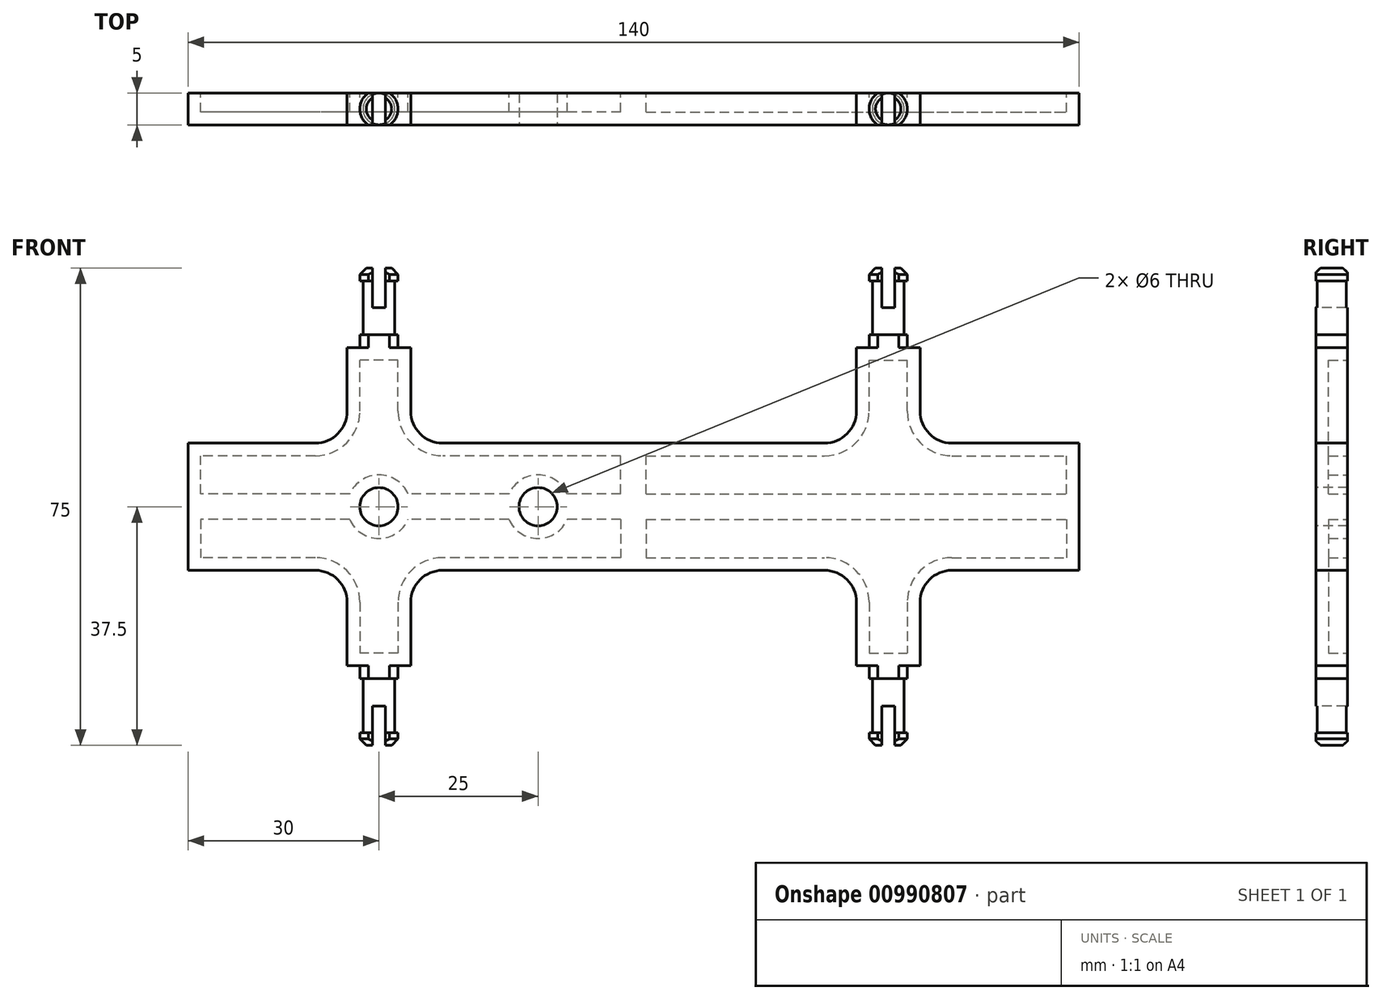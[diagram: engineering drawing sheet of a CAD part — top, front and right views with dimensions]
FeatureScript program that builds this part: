
annotation { "Feature Type Name" : "Feature", "Feature Type Description" : "" }
export const myFeature = defineFeature(function(context is Context, id is Id, definition is map)
    precondition{}
    {
        {
            var Q0;
            Q0=qCreatedBy(makeId("Front.planeOp"),FACE);
            var sketch = newSketch(context, id + "F0", { "sketchPlane" : qUnion([Q0])});
            skLineSegment(sketch, "E0.bottom", {"start": v(0, 0) * mm, "end": v(70, 0) * mm});
            skLineSegment(sketch, "E0.top", {"start": v(0, 10) * mm, "end": v(30, 10) * mm});
            skLineSegment(sketch, "E0.left", {"start": v(0, 0) * mm, "end": v(0, 10) * mm});
            skLineSegment(sketch, "E0.right", {"start": v(70, 0) * mm, "end": v(70, 10) * mm});
            skLineSegment(sketch, "E1.top", {"start": v(35, 25) * mm, "end": v(45, 25) * mm});
            skLineSegment(sketch, "E1.left", {"start": v(35, 15) * mm, "end": v(35, 25) * mm});
            skLineSegment(sketch, "E1.right", {"start": v(45, 15) * mm, "end": v(45, 25) * mm});
            skLineSegment(sketch, "E2.trimOffspring", {"start": v(50, 10) * mm, "end": v(70, 10) * mm});
            skPoint(sketch, "E3.visualSharp", {"position": v(35, 10) * mm});
            skArc(sketch, "E3.filletArc", {"start": v(30, 10) * mm, "mid": v(33.54, 11.46) * mm, "end": v(35, 15) * mm});
            skPoint(sketch, "E4.visualSharp", {"position": v(45, 10) * mm});
            skArc(sketch, "E4.filletArc", {"start": v(45, 15) * mm, "mid": v(46.46, 11.46) * mm, "end": v(50, 10) * mm});
            skSolve(sketch);
        }
        {
            var Q0;
            Q0 = qSketchRegion(id + "F0", true);
            extrude(context, id + "F1", {"entities" : qUnion([Q0]), "endBound" : BoundingType.SYMMETRIC, "depth" : 5 * mm, "offsetDistance" : 25 * mm});
        }
        {
            var Q0;
            Q0=makeQuery(id+"F1.opExtrude","CAP_FACE",FACE,{"disambiguationData":[OSD([sQuery(id+"F0.wireOp",EDGE,"E0.bottom"),sQuery(id+"F0.wireOp",EDGE,"E0.top"),sQuery(id+"F0.wireOp",EDGE,"E0.left"),sQuery(id+"F0.wireOp",EDGE,"E0.right"),sQuery(id+"F0.wireOp",EDGE,"E1.top"),sQuery(id+"F0.wireOp",EDGE,"E1.left"),sQuery(id+"F0.wireOp",EDGE,"E1.right"),sQuery(id+"F0.wireOp",EDGE,"E2.trimOffspring"),sQuery(id+"F0.wireOp",EDGE,"E3.filletArc"),sQuery(id+"F0.wireOp",EDGE,"E4.filletArc")])],"isStart":true});
            shell(context, id + "F2", {"entities" : qUnion([Q0]), "thickness" : 2 * mm});
        }
        {
            var Q0;
            Q0=qCreatedBy(makeId("Front.planeOp"),FACE);
            var sketch = newSketch(context, id + "F3", { "sketchPlane" : qUnion([Q0])});
            skLineSegment(sketch, "E5", {"start": v(40, 25) * mm, "end": v(40, 37.5) * mm});
            skLineSegment(sketch, "E6", {"start": v(40, 37.5) * mm, "end": v(43, 37.5) * mm});
            skLineSegment(sketch, "E7", {"start": v(43, 37.5) * mm, "end": v(43, 35.5) * mm});
            skLineSegment(sketch, "E8", {"start": v(43, 35.5) * mm, "end": v(42.5, 35.5) * mm});
            skLineSegment(sketch, "E9", {"start": v(42.5, 35.5) * mm, "end": v(42.5, 27) * mm});
            skLineSegment(sketch, "E10", {"start": v(42.5, 27) * mm, "end": v(43, 27) * mm});
            skLineSegment(sketch, "E11", {"start": v(43, 27) * mm, "end": v(43, 25) * mm});
            skLineSegment(sketch, "E12", {"start": v(43, 25) * mm, "end": v(40, 25) * mm});
            skSolve(sketch);
        }
        {
            var Q0;
            Q0=makeQuery(id+"F3.imprint","IMPRINT",FACE,{"disambiguationData":[TD([[makeQuery(id+"F3.imprint","IMPRINT",EDGE,{"derivedFrom":sQuery(id+"F3.wireOp",EDGE,"E5")}),-1.0]])]});
            var Q1;
            Q1=sQuery(id+"F3.wireOp",EDGE,"E5");
            revolve(context, id + "F4", {"operationType" : NewBodyOperationType.ADD, "surfaceOperationType" : NewSurfaceOperationType.NEW, "entities" : qUnion([Q0]), "axis" : qUnion([Q1]), "revolveType" : RevolveType.FULL});
        }
        {
            var Q0;
            Q0=makeQuery(id+"F4.opRevolve","SWEPT_EDGE",EDGE,{"disambiguationData":[OSD([sQuery(id+"F3.wireOp",EDGE,"E6"),sQuery(id+"F3.wireOp",EDGE,"E7")])]});
            chamfer(context, id + "F5", {"entities" : qUnion([Q0]), "width" : 1 * mm, "tangentPropagation" : true});
        }
        {
            var Q0;
            Q0=qCreatedBy(makeId("Top.planeOp"),FACE);
            var sketch = newSketch(context, id + "F6", { "sketchPlane" : qUnion([Q0])});
            skLineSegment(sketch, "E13.bottom", {"start": v(86.9, -2.5) * mm, "end": v(-83.1, -2.5) * mm});
            skLineSegment(sketch, "E13.top", {"start": v(86.9, 2.5) * mm, "end": v(-83.1, 2.5) * mm});
            skLineSegment(sketch, "E13.left", {"start": v(86.9, -2.5) * mm, "end": v(86.9, 2.5) * mm});
            skLineSegment(sketch, "E13.right", {"start": v(-83.1, -2.5) * mm, "end": v(-83.1, 2.5) * mm});
            skSolve(sketch);
        }
        {
            var Q0;
            Q0 = qSketchRegion(id + "F6", true);
            extrude(context, id + "F7", {"entities" : qUnion([Q0]), "operationType" : NewBodyOperationType.INTERSECT, "endBound" : BoundingType.THROUGH_ALL, "depth" : 50 * mm, "offsetDistance" : 25 * mm});
        }
        {
            var Q0;
            Q0=qCreatedBy(makeId("Top.planeOp"),FACE);
            cPlane(context, id + "F8", {"entities" : qUnion([Q0]), "cplaneType" : CPlaneType.OFFSET, "offset" : 37.6 * mm, "width" : 150 * mm, "height" : 150 * mm});
        }
        {
            var Q0;
            Q0=qCreatedBy(id+"F8.planeOp",FACE);
            var sketch = newSketch(context, id + "F9", { "sketchPlane" : qUnion([Q0])});
            skLineSegment(sketch, "E14.bottom", {"start": v(39, 5.25) * mm, "end": v(41, 5.25) * mm});
            skLineSegment(sketch, "E14.top", {"start": v(39, -5.25) * mm, "end": v(41, -5.25) * mm});
            skLineSegment(sketch, "E14.left", {"start": v(39, 5.25) * mm, "end": v(39, -5.25) * mm});
            skLineSegment(sketch, "E14.right", {"start": v(41, 5.25) * mm, "end": v(41, -5.25) * mm});
            skSolve(sketch);
        }
        {
            var Q0;
            Q0 = qSketchRegion(id + "F9", true);
            extrude(context, id + "F10", {"entities" : qUnion([Q0]), "operationType" : NewBodyOperationType.REMOVE, "oppositeDirection" : true, "depth" : 6.3 * mm, "offsetDistance" : 25 * mm});
        }
        {
            var Q0;
            Q0=makeQuery(id+"F1.opExtrude","SWEPT_BODY",BODY,{"disambiguationData":[OSD([sQuery(id+"F0.wireOp",EDGE,"E0.bottom"),sQuery(id+"F0.wireOp",EDGE,"E0.top"),sQuery(id+"F0.wireOp",EDGE,"E0.left"),sQuery(id+"F0.wireOp",EDGE,"E0.right"),sQuery(id+"F0.wireOp",EDGE,"E1.top"),sQuery(id+"F0.wireOp",EDGE,"E1.left"),sQuery(id+"F0.wireOp",EDGE,"E1.right"),sQuery(id+"F0.wireOp",EDGE,"E2.trimOffspring"),sQuery(id+"F0.wireOp",EDGE,"E3.filletArc"),sQuery(id+"F0.wireOp",EDGE,"E4.filletArc")])]});
            var Q1;
            Q1=qCreatedBy(makeId("Top.planeOp"),FACE);
            mirror(context, id + "F11", {"operationType" : NewBodyOperationType.ADD, "entities" : qUnion([Q0]), "mirrorPlane" : qUnion([Q1])});
        }
        {
            var Q0;
            Q0=makeQuery(id+"F1.opExtrude","SWEPT_BODY",BODY,{"disambiguationData":[OSD([sQuery(id+"F0.wireOp",EDGE,"E0.bottom"),sQuery(id+"F0.wireOp",EDGE,"E0.top"),sQuery(id+"F0.wireOp",EDGE,"E0.left"),sQuery(id+"F0.wireOp",EDGE,"E0.right"),sQuery(id+"F0.wireOp",EDGE,"E1.top"),sQuery(id+"F0.wireOp",EDGE,"E1.left"),sQuery(id+"F0.wireOp",EDGE,"E1.right"),sQuery(id+"F0.wireOp",EDGE,"E2.trimOffspring"),sQuery(id+"F0.wireOp",EDGE,"E3.filletArc"),sQuery(id+"F0.wireOp",EDGE,"E4.filletArc")])]});
            var Q1;
            Q1=qCreatedBy(makeId("Right.planeOp"),FACE);
            mirror(context, id + "F12", {"operationType" : NewBodyOperationType.ADD, "entities" : qUnion([Q0]), "mirrorPlane" : qUnion([Q1])});
        }
        {
            var Q0;
            Q0=qCreatedBy(makeId("Front.planeOp"),FACE);
            var sketch = newSketch(context, id + "F13", { "sketchPlane" : qUnion([Q0])});
            skCircle(sketch, "E15", {"center": v(-40, 0) * mm, "radius": 5 * mm});
            skCircle(sketch, "E16", {"center": v(-15, 0) * mm, "radius": 5 * mm});
            skSolve(sketch);
        }
        {
            var Q0;
            Q0 = qSketchRegion(id + "F13", true);
            extrude(context, id + "F14", {"entities" : qUnion([Q0]), "operationType" : NewBodyOperationType.ADD, "endBound" : BoundingType.SYMMETRIC, "depth" : 5 * mm, "offsetDistance" : 25 * mm});
        }
        {
            var Q0;
            Q0=qCreatedBy(makeId("Front.planeOp"),FACE);
            cPlane(context, id + "F15", {"entities" : qUnion([Q0]), "cplaneType" : CPlaneType.OFFSET, "offset" : 10 * mm, "width" : 150 * mm, "height" : 150 * mm});
        }
        {
            var Q0;
            Q0=qCreatedBy(id+"F15.planeOp",FACE);
            var sketch = newSketch(context, id + "F16", { "sketchPlane" : qUnion([Q0])});
            skPoint(sketch, "E17", {"position": v(-15, 0) * mm});
            skPoint(sketch, "E18", {"position": v(-40, 0) * mm});
            skSolve(sketch);
        }
        {
            var Q0;
            Q0=sQuery(id+"F16.wireOp",VERTEX,"E18");
            var Q1;
            Q1=sQuery(id+"F16.wireOp",VERTEX,"E17");
            var Q2;
            Q2=makeQuery(id+"F1.opExtrude","SWEPT_BODY",BODY,{"disambiguationData":[OSD([sQuery(id+"F0.wireOp",EDGE,"E0.bottom"),sQuery(id+"F0.wireOp",EDGE,"E0.top"),sQuery(id+"F0.wireOp",EDGE,"E0.left"),sQuery(id+"F0.wireOp",EDGE,"E0.right"),sQuery(id+"F0.wireOp",EDGE,"E1.top"),sQuery(id+"F0.wireOp",EDGE,"E1.left"),sQuery(id+"F0.wireOp",EDGE,"E1.right"),sQuery(id+"F0.wireOp",EDGE,"E2.trimOffspring"),sQuery(id+"F0.wireOp",EDGE,"E3.filletArc"),sQuery(id+"F0.wireOp",EDGE,"E4.filletArc")])]});
            hole(context, id + "F17", {"style" : HoleStyle.SIMPLE, "endStyle" : HoleEndStyle.THROUGH, "holeDiameter" : 6 * mm, "majorDiameter" : 5 * mm, "isTappedThrough" : true, "tappedDepth" : 12 * mm, "tapClearance" : 3, "locations" : qUnion([Q0, Q1]), "scope" : qUnion([Q2])});
        }
    });
